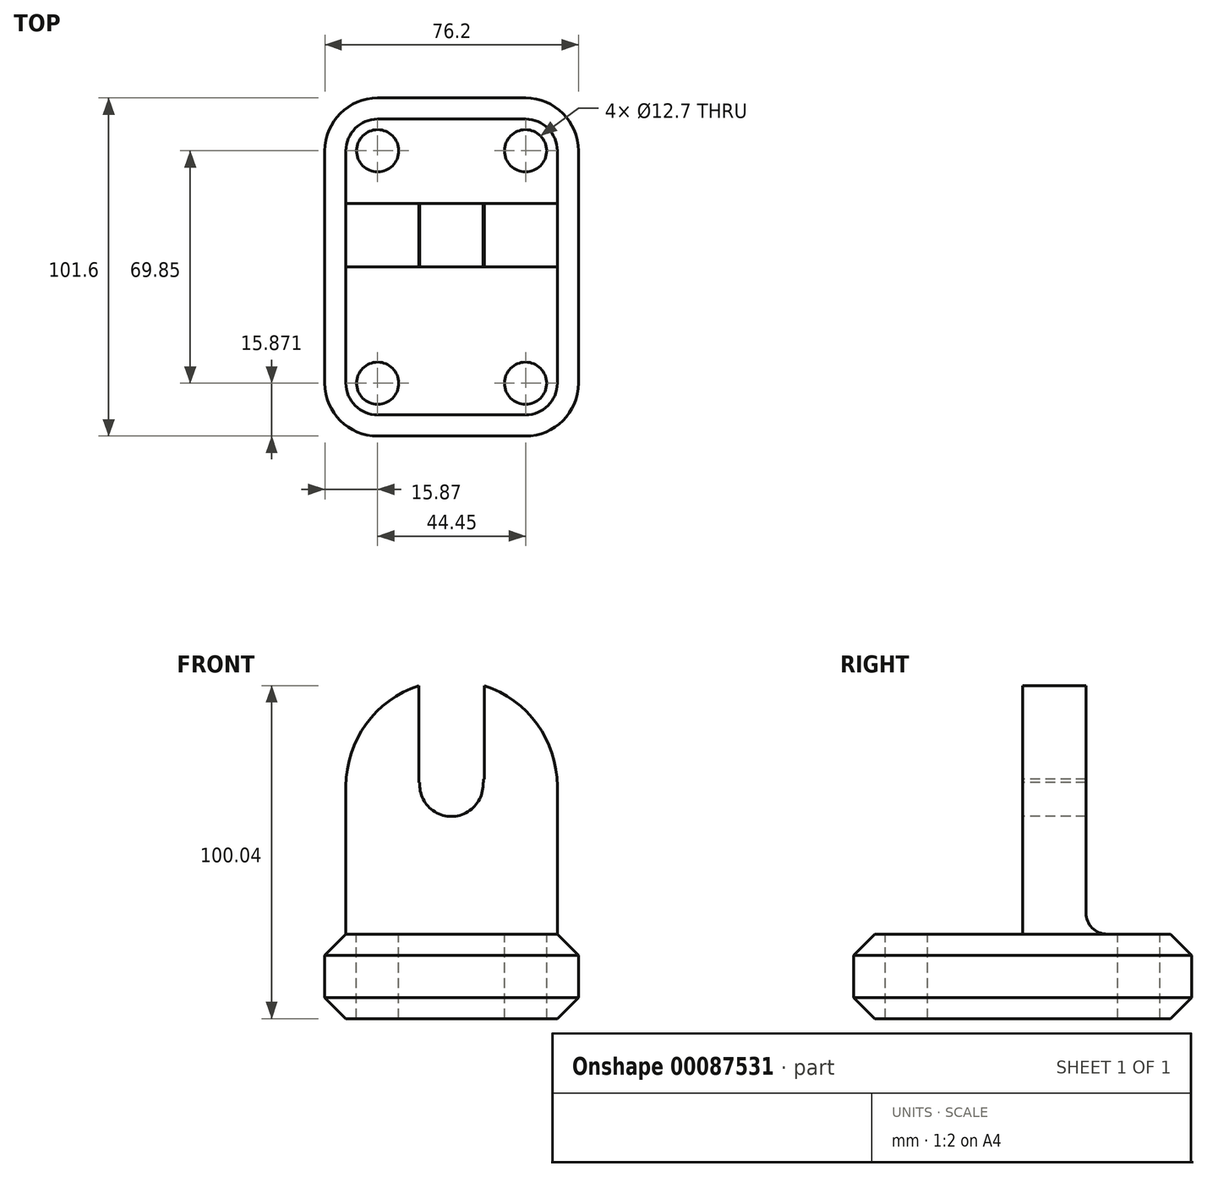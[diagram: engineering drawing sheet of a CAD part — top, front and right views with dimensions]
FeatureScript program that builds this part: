
annotation { "Feature Type Name" : "Feature", "Feature Type Description" : "" }
export const myFeature = defineFeature(function(context is Context, id is Id, definition is map)
    precondition{}
    {
        {
            var Q0;
            Q0=qCreatedBy(makeId("Top.planeOp"),FACE);
            var sketch = newSketch(context, id + "F0", { "sketchPlane" : qUnion([Q0])});
            skLineSegment(sketch, "E0.bottom", {"start": v(-57.1, 57.86) * mm, "end": v(19.1, 57.86) * mm});
            skLineSegment(sketch, "E0.top", {"start": v(-57.1, -43.74) * mm, "end": v(19.1, -43.74) * mm});
            skLineSegment(sketch, "E0.left", {"start": v(-57.1, 57.86) * mm, "end": v(-57.1, -43.74) * mm});
            skLineSegment(sketch, "E0.right", {"start": v(19.1, 57.86) * mm, "end": v(19.1, -43.74) * mm});
            skSolve(sketch);
        }
        {
            var Q0;
            Q0 = qSketchRegion(id + "F0", true);
            extrude(context, id + "F1", {"entities" : qUnion([Q0]), "depth" : 25.4 * mm});
        }
        {
            var Q0;
            Q0=makeQuery(id+"F1.opExtrude","CAP_FACE",FACE,{"disambiguationData":[OSD([sQuery(id+"F0.wireOp",EDGE,"E0.bottom"),sQuery(id+"F0.wireOp",EDGE,"E0.top"),sQuery(id+"F0.wireOp",EDGE,"E0.left"),sQuery(id+"F0.wireOp",EDGE,"E0.right")])],"isStart":false});
            var sketch = newSketch(context, id + "F2", { "sketchPlane" : qUnion([Q0])});
            skCircle(sketch, "E1", {"center": v(-41.22, 41.98) * mm, "radius": 6.35 * mm});
            skCircle(sketch, "E2", {"center": v(3.23, 41.98) * mm, "radius": 6.35 * mm});
            skCircle(sketch, "E3", {"center": v(-41.22, -27.87) * mm, "radius": 6.35 * mm});
            skCircle(sketch, "E4", {"center": v(3.23, -27.87) * mm, "radius": 6.35 * mm});
            skSolve(sketch);
        }
        {
            var Q0;
            Q0 = qSketchRegion(id + "F2", true);
            extrude(context, id + "F3", {"entities" : qUnion([Q0]), "operationType" : NewBodyOperationType.REMOVE, "endBound" : BoundingType.THROUGH_ALL, "oppositeDirection" : true, "depth" : 25.4 * mm});
        }
        {
            var Q0;
            Q0=makeQuery(id+"F1.opExtrude","SWEPT_EDGE",EDGE,{"disambiguationData":[OSD([sQuery(id+"F0.wireOp",EDGE,"E0.top"),sQuery(id+"F0.wireOp",EDGE,"E0.left")])]});
            var Q1;
            Q1=makeQuery(id+"F1.opExtrude","SWEPT_EDGE",EDGE,{"disambiguationData":[OSD([sQuery(id+"F0.wireOp",EDGE,"E0.top"),sQuery(id+"F0.wireOp",EDGE,"E0.right")])]});
            var Q2;
            Q2=makeQuery(id+"F1.opExtrude","SWEPT_EDGE",EDGE,{"disambiguationData":[OSD([sQuery(id+"F0.wireOp",EDGE,"E0.bottom"),sQuery(id+"F0.wireOp",EDGE,"E0.left")])]});
            var Q3;
            Q3=makeQuery(id+"F1.opExtrude","SWEPT_EDGE",EDGE,{"disambiguationData":[OSD([sQuery(id+"F0.wireOp",EDGE,"E0.bottom"),sQuery(id+"F0.wireOp",EDGE,"E0.right")])]});
            fillet(context, id + "F4", {"entities" : qUnion([Q0, Q1, Q2, Q3]), "radius" : 15.88 * mm, "tangentPropagation" : true, "allowEdgeOverflow" : false});
        }
        {
            var Q0;
            Q0=makeQuery(id+"F1.opExtrude","SWEPT_FACE",FACE,{"disambiguationData":[OSD([sQuery(id+"F0.wireOp",EDGE,"E0.right")])]});
            var Q1;
            Q1=makeQuery(id+"F1.opExtrude","SWEPT_FACE",FACE,{"disambiguationData":[OSD([sQuery(id+"F0.wireOp",EDGE,"E0.left")])]});
            chamfer(context, id + "F5", {"entities" : qUnion([Q0, Q1]), "width" : 6.35 * mm, "tangentPropagation" : true});
        }
        {
            var Q0;
            Q0=makeQuery(id+"F1.opExtrude","CAP_FACE",FACE,{"disambiguationData":[OSD([sQuery(id+"F0.wireOp",EDGE,"E0.bottom"),sQuery(id+"F0.wireOp",EDGE,"E0.top"),sQuery(id+"F0.wireOp",EDGE,"E0.left"),sQuery(id+"F0.wireOp",EDGE,"E0.right")])],"isStart":false});
            var sketch = newSketch(context, id + "F6", { "sketchPlane" : qUnion([Q0])});
            skLineSegment(sketch, "E5.bottom", {"start": v(-50.74, 26.1) * mm, "end": v(12.76, 26.1) * mm});
            skLineSegment(sketch, "E5.top", {"start": v(-50.74, 7.06) * mm, "end": v(12.76, 7.06) * mm});
            skLineSegment(sketch, "E5.left", {"start": v(-50.74, 26.1) * mm, "end": v(-50.74, 7.06) * mm});
            skLineSegment(sketch, "E5.right", {"start": v(12.76, 26.1) * mm, "end": v(12.76, 7.06) * mm});
            skSolve(sketch);
        }
        {
            var Q0;
            Q0 = qSketchRegion(id + "F6", true);
            extrude(context, id + "F7", {"entities" : qUnion([Q0]), "operationType" : NewBodyOperationType.ADD, "depth" : 76.2 * mm});
        }
        {
            var Q0;
            Q0=makeQuery(id+"F7.opExtrude","CAP_EDGE",EDGE,{"disambiguationData":[OSD([sQuery(id+"F6.wireOp",EDGE,"E5.top")])],"isStart":true});
            var Q1;
            Q1=makeQuery(id+"F7.opExtrude","CAP_EDGE",EDGE,{"disambiguationData":[OSD([sQuery(id+"F6.wireOp",EDGE,"E5.bottom")])],"isStart":true});
            fillet(context, id + "F8", {"entities" : qUnion([Q0, Q1]), "radius" : 6.35 * mm, "tangentPropagation" : true, "allowEdgeOverflow" : false});
        }
        {
            var Q0;
            Q0=makeQuery(id+"F7.opExtrude","CAP_EDGE",EDGE,{"disambiguationData":[OSD([sQuery(id+"F6.wireOp",EDGE,"E5.left")])],"isStart":false});
            var Q1;
            Q1=makeQuery(id+"F7.opExtrude","CAP_EDGE",EDGE,{"disambiguationData":[OSD([sQuery(id+"F6.wireOp",EDGE,"E5.right")])],"isStart":false});
            fillet(context, id + "F9", {"entities" : qUnion([Q0, Q1]), "radius" : 31.75 * mm, "tangentPropagation" : true, "allowEdgeOverflow" : false});
        }
        {
            var Q0;
            Q0=makeQuery(id+"F7.opExtrude","SWEPT_FACE",FACE,{"disambiguationData":[OSD([sQuery(id+"F6.wireOp",EDGE,"E5.top")])]});
            var sketch = newSketch(context, id + "F10", { "sketchPlane" : qUnion([Q0])});
            skLineSegment(sketch, "E6", {"start": v(12.76, 31.75) * mm, "end": v(12.76, 69.85) * mm});
            skSolve(sketch);
        }
        {
            var Q0;
            Q0=makeQuery(id+"F10.imprint","IMPRINT",FACE,{"disambiguationData":[TD([[makeQuery(id+"F10.imprint","IMPRINT",EDGE,{"derivedFrom":sQuery(id+"F10.wireOp",EDGE,"E6")}),-1.0]])]});
            var sketch = newSketch(context, id + "F11", { "sketchPlane" : qUnion([Q0])});
            skCircle(sketch, "E7", {"center": v(-19.1, 86.14) * mm, "radius": 17.52 * mm});
            skSolve(sketch);
        }
        {
            var Q0;
            {var subQ0=sQuery(id+"F11.wireOp",EDGE,"E7");var subQ1=makeQuery(id+"F10.imprint","IMPRINT",EDGE,{"derivedFrom":makeQuery(id+"F9.opFillet","BLEND_EDGE",EDGE,{"blendedFrom":[makeQuery(id+"F7.opExtrude","CAP_EDGE",EDGE,{"disambiguationData":[OSD([sQuery(id+"F6.wireOp",EDGE,"E5.right")])],"isStart":false}),makeQuery(id+"F7.opExtrude","SWEPT_FACE",FACE,{"disambiguationData":[OSD([sQuery(id+"F6.wireOp",EDGE,"E5.top")])]})],"blendedInto":[makeQuery(id+"F7.opExtrude","SWEPT_FACE",FACE,{"disambiguationData":[OSD([sQuery(id+"F6.wireOp",EDGE,"E5.top")])]})]})});var subQ2=makeQuery(id+"F11.imprint","INTERSECT",VERTEX,{"disambiguationData":[OD(0.0)],"derivedFrom":[subQ1,subQ0]});Q0=makeQuery(id+"F11.imprint","IMPRINT",FACE,{"disambiguationData":[TD([[makeQuery(id+"F11.imprint","IMPRINT",EDGE,{"disambiguationData":[TD([[subQ2,-1.0]])],"derivedFrom":subQ0}),1.0]])]});}
            extrude(context, id + "F12", {"entities" : qUnion([Q0]), "operationType" : NewBodyOperationType.ADD, "oppositeDirection" : true, "depth" : 19.05 * mm});
        }
        {
            var Q0;
            Q0=makeQuery(id+"F10.imprint","IMPRINT",FACE,{"disambiguationData":[TD([[makeQuery(id+"F10.imprint","IMPRINT",EDGE,{"derivedFrom":sQuery(id+"F10.wireOp",EDGE,"E6")}),-1.0]])]});
            var sketch = newSketch(context, id + "F13", { "sketchPlane" : qUnion([Q0])});
            skLineSegment(sketch, "E8", {"start": v(11.82, 31.61) * mm, "end": v(-19.93, 31.61) * mm});
            skSolve(sketch);
        }
        {
            var Q0;
            Q0=makeQuery(id+"F13.imprint","IMPRINT",FACE,{"disambiguationData":[TD([[makeQuery(id+"F13.imprint","IMPRINT",EDGE,{"derivedFrom":makeQuery(id+"F10.imprint","IMPRINT",EDGE,{"derivedFrom":sQuery(id+"F10.wireOp",EDGE,"E6")})}),-1.0]])]});
            var sketch = newSketch(context, id + "F14", { "sketchPlane" : qUnion([Q0])});
            skCircle(sketch, "E9", {"center": v(-19.07, 70.26) * mm, "radius": 9.53 * mm});
            skLineSegment(sketch, "E10.bottom", {"start": v(-28.31, 72.56) * mm, "end": v(-9.94, 72.56) * mm});
            skLineSegment(sketch, "E10.top", {"start": v(-28.31, 102.17) * mm, "end": v(-9.94, 102.17) * mm});
            skLineSegment(sketch, "E10.left", {"start": v(-28.31, 72.56) * mm, "end": v(-28.31, 102.17) * mm});
            skLineSegment(sketch, "E10.right", {"start": v(-9.94, 72.56) * mm, "end": v(-9.94, 102.17) * mm});
            skSolve(sketch);
        }
        {
            var Q0;
            Q0 = qSketchRegion(id + "F14", true);
            extrude(context, id + "F15", {"entities" : qUnion([Q0]), "operationType" : NewBodyOperationType.REMOVE, "oppositeDirection" : true, "depth" : 19.05 * mm});
        }
        {
            var Q0;
            Q0=makeQuery(id+"F13.imprint","IMPRINT",FACE,{"disambiguationData":[TD([[makeQuery(id+"F13.imprint","IMPRINT",EDGE,{"derivedFrom":makeQuery(id+"F10.imprint","IMPRINT",EDGE,{"derivedFrom":sQuery(id+"F10.wireOp",EDGE,"E6")})}),-1.0]])]});
            var sketch = newSketch(context, id + "F16", { "sketchPlane" : qUnion([Q0])});
            skLineSegment(sketch, "E11.bottom", {"start": v(-28.6, 71.71) * mm, "end": v(-9.88, 71.71) * mm});
            skLineSegment(sketch, "E11.top", {"start": v(-28.6, 100.27) * mm, "end": v(-9.88, 100.27) * mm});
            skLineSegment(sketch, "E11.left", {"start": v(-28.6, 71.71) * mm, "end": v(-28.6, 100.27) * mm});
            skLineSegment(sketch, "E11.right", {"start": v(-9.88, 71.71) * mm, "end": v(-9.88, 100.27) * mm});
            skSolve(sketch);
        }
        {
            var Q0;
            Q0 = qSketchRegion(id + "F16", true);
            extrude(context, id + "F17", {"entities" : qUnion([Q0]), "operationType" : NewBodyOperationType.REMOVE, "oppositeDirection" : true, "depth" : 19.05 * mm});
        }
        {
            var Q0;
            Q0=makeQuery(id+"F13.imprint","IMPRINT",FACE,{"disambiguationData":[TD([[makeQuery(id+"F13.imprint","IMPRINT",EDGE,{"derivedFrom":makeQuery(id+"F10.imprint","IMPRINT",EDGE,{"derivedFrom":sQuery(id+"F10.wireOp",EDGE,"E6")})}),-1.0]])]});
            var sketch = newSketch(context, id + "F18", { "sketchPlane" : qUnion([Q0])});
            skLineSegment(sketch, "E12.bottom", {"start": v(-28.83, 71.47) * mm, "end": v(-9.64, 71.47) * mm});
            skLineSegment(sketch, "E12.top", {"start": v(-28.83, 101.95) * mm, "end": v(-9.64, 101.95) * mm});
            skLineSegment(sketch, "E12.left", {"start": v(-28.83, 71.47) * mm, "end": v(-28.83, 101.95) * mm});
            skLineSegment(sketch, "E12.right", {"start": v(-9.64, 71.47) * mm, "end": v(-9.64, 101.95) * mm});
            skSolve(sketch);
        }
        {
            var Q0;
            Q0 = qSketchRegion(id + "F18", true);
            extrude(context, id + "F19", {"entities" : qUnion([Q0]), "operationType" : NewBodyOperationType.REMOVE, "oppositeDirection" : true, "depth" : 19.05 * mm});
        }
        {
            var Q0;
            Q0=makeQuery(id+"F13.imprint","IMPRINT",FACE,{"disambiguationData":[TD([[makeQuery(id+"F13.imprint","IMPRINT",EDGE,{"derivedFrom":makeQuery(id+"F10.imprint","IMPRINT",EDGE,{"derivedFrom":sQuery(id+"F10.wireOp",EDGE,"E6")})}),-1.0]])]});
            var sketch = newSketch(context, id + "F20", { "sketchPlane" : qUnion([Q0])});
            skLineSegment(sketch, "E13.bottom", {"start": v(-28.83, 71) * mm, "end": v(-9.4, 71) * mm});
            skLineSegment(sketch, "E13.top", {"start": v(-28.83, 103.87) * mm, "end": v(-9.4, 103.87) * mm});
            skLineSegment(sketch, "E13.left", {"start": v(-28.83, 71) * mm, "end": v(-28.83, 103.87) * mm});
            skLineSegment(sketch, "E13.right", {"start": v(-9.4, 71) * mm, "end": v(-9.4, 103.87) * mm});
            skSolve(sketch);
        }
        {
            var Q0;
            Q0 = qSketchRegion(id + "F20", true);
            extrude(context, id + "F21", {"entities" : qUnion([Q0]), "operationType" : NewBodyOperationType.REMOVE, "oppositeDirection" : true, "depth" : 19.05 * mm});
        }
        {
            var Q0;
            Q0=makeQuery(id+"F13.imprint","IMPRINT",FACE,{"disambiguationData":[TD([[makeQuery(id+"F13.imprint","IMPRINT",EDGE,{"derivedFrom":makeQuery(id+"F10.imprint","IMPRINT",EDGE,{"derivedFrom":sQuery(id+"F10.wireOp",EDGE,"E6")})}),-1.0]])]});
            var sketch = newSketch(context, id + "F22", { "sketchPlane" : qUnion([Q0])});
            skLineSegment(sketch, "E14.bottom", {"start": v(-9.16, 71.95) * mm, "end": v(-28.6, 71.95) * mm});
            skLineSegment(sketch, "E14.top", {"start": v(-9.16, 101.95) * mm, "end": v(-28.6, 101.95) * mm});
            skLineSegment(sketch, "E14.left", {"start": v(-9.16, 71.95) * mm, "end": v(-9.16, 101.95) * mm});
            skLineSegment(sketch, "E14.right", {"start": v(-28.6, 71.95) * mm, "end": v(-28.6, 101.95) * mm});
            skSolve(sketch);
        }
        {
            var Q0;
            Q0 = qSketchRegion(id + "F22", true);
            extrude(context, id + "F23", {"entities" : qUnion([Q0]), "operationType" : NewBodyOperationType.REMOVE, "oppositeDirection" : true, "depth" : 19.05 * mm});
        }
        {
            var Q0;
            Q0=makeQuery(id+"F13.imprint","IMPRINT",FACE,{"disambiguationData":[TD([[makeQuery(id+"F13.imprint","IMPRINT",EDGE,{"derivedFrom":makeQuery(id+"F10.imprint","IMPRINT",EDGE,{"derivedFrom":sQuery(id+"F10.wireOp",EDGE,"E6")})}),-1.0]])]});
            var sketch = newSketch(context, id + "F24", { "sketchPlane" : qUnion([Q0])});
            skLineSegment(sketch, "E15.bottom", {"start": v(-9.16, 72.43) * mm, "end": v(-28.6, 72.43) * mm});
            skLineSegment(sketch, "E15.top", {"start": v(-9.16, 102.19) * mm, "end": v(-28.6, 102.19) * mm});
            skLineSegment(sketch, "E15.left", {"start": v(-9.16, 72.43) * mm, "end": v(-9.16, 102.19) * mm});
            skLineSegment(sketch, "E15.right", {"start": v(-28.6, 72.43) * mm, "end": v(-28.6, 102.19) * mm});
            skSolve(sketch);
        }
        {
            var Q0;
            Q0 = qSketchRegion(id + "F24", true);
            extrude(context, id + "F25", {"entities" : qUnion([Q0]), "operationType" : NewBodyOperationType.REMOVE, "oppositeDirection" : true, "depth" : 19.05 * mm});
        }
    });
